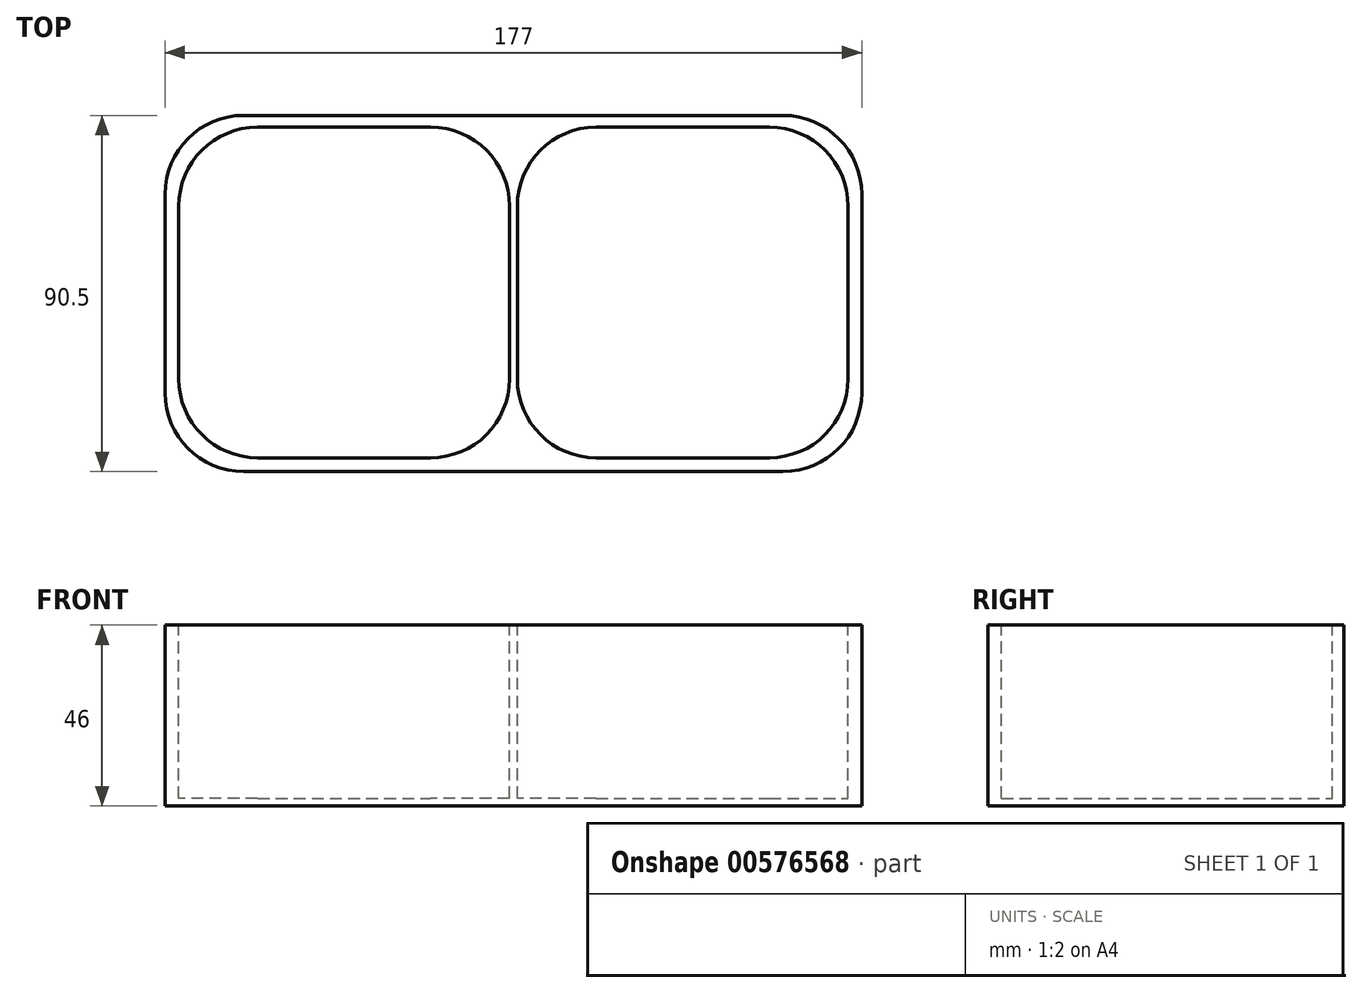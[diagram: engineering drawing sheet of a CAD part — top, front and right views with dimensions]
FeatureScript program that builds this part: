
annotation { "Feature Type Name" : "Feature", "Feature Type Description" : "" }
export const myFeature = defineFeature(function(context is Context, id is Id, definition is map)
    precondition{}
    {
        {
            var Q0;
            Q0=qCreatedBy(makeId("Top.planeOp"),FACE);
            var sketch = newSketch(context, id + "F0", { "sketchPlane" : qUnion([Q0])});
            skLineSegment(sketch, "E0.bottom", {"start": v(-97.24, 18.33) * mm, "end": v(-12.74, 18.33) * mm, "construction": true});
            skLineSegment(sketch, "E0.top", {"start": v(-97.24, -66.17) * mm, "end": v(-12.74, -66.17) * mm, "construction": true});
            skLineSegment(sketch, "E0.left", {"start": v(-97.24, 18.33) * mm, "end": v(-97.24, -66.17) * mm, "construction": true});
            skLineSegment(sketch, "E0.right", {"start": v(-12.74, 18.33) * mm, "end": v(-12.74, -66.17) * mm, "construction": true});
            skLineSegment(sketch, "E1.bottom", {"start": v(-10.74, 18.33) * mm, "end": v(73.76, 18.33) * mm, "construction": true});
            skLineSegment(sketch, "E1.top", {"start": v(-10.74, -66.17) * mm, "end": v(73.76, -66.17) * mm, "construction": true});
            skLineSegment(sketch, "E1.left", {"start": v(-10.74, 18.33) * mm, "end": v(-10.74, -66.17) * mm, "construction": true});
            skLineSegment(sketch, "E1.right", {"start": v(73.76, 18.33) * mm, "end": v(73.76, -66.17) * mm, "construction": true});
            skLineSegment(sketch, "E2.bottom", {"start": v(-100.24, 21.33) * mm, "end": v(76.76, 21.33) * mm});
            skLineSegment(sketch, "E2.top", {"start": v(-100.24, -69.17) * mm, "end": v(76.76, -69.17) * mm});
            skLineSegment(sketch, "E2.left", {"start": v(-100.24, 21.33) * mm, "end": v(-100.24, -69.17) * mm});
            skLineSegment(sketch, "E2.right", {"start": v(76.76, 21.33) * mm, "end": v(76.76, -69.17) * mm});
            skSolve(sketch);
        }
        {
            var Q0;
            Q0=makeQuery(id+"F0.imprint","IMPRINT",FACE,{"disambiguationData":[TD([[makeQuery(id+"F0.imprint","IMPRINT",EDGE,{"derivedFrom":sQuery(id+"F0.wireOp",EDGE,"E2.bottom")}),-1.0]])]});
            extrude(context, id + "F1", {"entities" : qUnion([Q0]), "oppositeDirection" : true, "depth" : 46 * mm, "offsetDistance" : 25 * mm});
        }
        {
            var Q0;
            Q0=makeQuery(id+"F1.opExtrude","CAP_FACE",FACE,{"disambiguationData":[OSD([sQuery(id+"F0.wireOp",EDGE,"E2.bottom"),sQuery(id+"F0.wireOp",EDGE,"E2.top"),sQuery(id+"F0.wireOp",EDGE,"E2.left"),sQuery(id+"F0.wireOp",EDGE,"E2.right")])],"isStart":true});
            var sketch = newSketch(context, id + "F2", { "sketchPlane" : qUnion([Q0])});
            skLineSegment(sketch, "E3.bottom", {"start": v(-96.74, 18.33) * mm, "end": v(-12.74, 18.33) * mm});
            skLineSegment(sketch, "E3.top", {"start": v(-96.74, -65.67) * mm, "end": v(-12.74, -65.67) * mm});
            skLineSegment(sketch, "E3.left", {"start": v(-96.74, 18.33) * mm, "end": v(-96.74, -65.67) * mm});
            skLineSegment(sketch, "E3.right", {"start": v(-12.74, 18.33) * mm, "end": v(-12.74, -65.67) * mm});
            skLineSegment(sketch, "E4.bottom", {"start": v(-10.74, -65.67) * mm, "end": v(73.26, -65.67) * mm});
            skLineSegment(sketch, "E4.top", {"start": v(-10.74, 18.33) * mm, "end": v(73.26, 18.33) * mm});
            skLineSegment(sketch, "E4.left", {"start": v(-10.74, -65.67) * mm, "end": v(-10.74, 18.33) * mm});
            skLineSegment(sketch, "E4.right", {"start": v(73.26, -65.67) * mm, "end": v(73.26, 18.33) * mm});
            skSolve(sketch);
        }
        {
            var Q0;
            Q0 = qSketchRegion(id + "F2", true);
            extrude(context, id + "F3", {"entities" : qUnion([Q0]), "operationType" : NewBodyOperationType.REMOVE, "oppositeDirection" : true, "depth" : 44 * mm, "offsetDistance" : 25 * mm});
        }
        {
            var Q0;
            Q0=makeQuery(id+"F3.boolean.opBoolean","COPY",EDGE,{"derivedFrom":makeQuery(id+"F3.opExtrude","SWEPT_EDGE",EDGE,{"disambiguationData":[OSD([sQuery(id+"F2.wireOp",EDGE,"E3.bottom"),sQuery(id+"F2.wireOp",EDGE,"E3.left")])]})});
            var Q1;
            Q1=makeQuery(id+"F3.boolean.opBoolean","COPY",EDGE,{"derivedFrom":makeQuery(id+"F3.opExtrude","SWEPT_EDGE",EDGE,{"disambiguationData":[OSD([sQuery(id+"F2.wireOp",EDGE,"E3.top"),sQuery(id+"F2.wireOp",EDGE,"E3.left")])]})});
            var Q2;
            Q2=makeQuery(id+"F3.boolean.opBoolean","COPY",EDGE,{"derivedFrom":makeQuery(id+"F3.opExtrude","SWEPT_EDGE",EDGE,{"disambiguationData":[OSD([sQuery(id+"F2.wireOp",EDGE,"E3.top"),sQuery(id+"F2.wireOp",EDGE,"E3.right")])]})});
            var Q3;
            Q3=makeQuery(id+"F3.boolean.opBoolean","COPY",EDGE,{"derivedFrom":makeQuery(id+"F3.opExtrude","SWEPT_EDGE",EDGE,{"disambiguationData":[OSD([sQuery(id+"F2.wireOp",EDGE,"E3.bottom"),sQuery(id+"F2.wireOp",EDGE,"E3.right")])]})});
            var Q4;
            Q4=makeQuery(id+"F3.boolean.opBoolean","COPY",EDGE,{"derivedFrom":makeQuery(id+"F3.opExtrude","SWEPT_EDGE",EDGE,{"disambiguationData":[OSD([sQuery(id+"F2.wireOp",EDGE,"E4.top"),sQuery(id+"F2.wireOp",EDGE,"E4.left")])]})});
            var Q5;
            Q5=makeQuery(id+"F3.boolean.opBoolean","COPY",EDGE,{"derivedFrom":makeQuery(id+"F3.opExtrude","SWEPT_EDGE",EDGE,{"disambiguationData":[OSD([sQuery(id+"F2.wireOp",EDGE,"E4.bottom"),sQuery(id+"F2.wireOp",EDGE,"E4.left")])]})});
            var Q6;
            Q6=makeQuery(id+"F3.boolean.opBoolean","COPY",EDGE,{"derivedFrom":makeQuery(id+"F3.opExtrude","SWEPT_EDGE",EDGE,{"disambiguationData":[OSD([sQuery(id+"F2.wireOp",EDGE,"E4.top"),sQuery(id+"F2.wireOp",EDGE,"E4.right")])]})});
            var Q7;
            Q7=makeQuery(id+"F3.boolean.opBoolean","COPY",EDGE,{"derivedFrom":makeQuery(id+"F3.opExtrude","SWEPT_EDGE",EDGE,{"disambiguationData":[OSD([sQuery(id+"F2.wireOp",EDGE,"E4.bottom"),sQuery(id+"F2.wireOp",EDGE,"E4.right")])]})});
            var Q8;
            Q8=makeQuery(id+"F1.opExtrude","SWEPT_EDGE",EDGE,{"disambiguationData":[OSD([sQuery(id+"F0.wireOp",EDGE,"E2.bottom"),sQuery(id+"F0.wireOp",EDGE,"E2.right")])]});
            var Q9;
            Q9=makeQuery(id+"F1.opExtrude","SWEPT_EDGE",EDGE,{"disambiguationData":[OSD([sQuery(id+"F0.wireOp",EDGE,"E2.bottom"),sQuery(id+"F0.wireOp",EDGE,"E2.left")])]});
            var Q10;
            Q10=makeQuery(id+"F1.opExtrude","SWEPT_EDGE",EDGE,{"disambiguationData":[OSD([sQuery(id+"F0.wireOp",EDGE,"E2.top"),sQuery(id+"F0.wireOp",EDGE,"E2.left")])]});
            var Q11;
            Q11=makeQuery(id+"F1.opExtrude","SWEPT_EDGE",EDGE,{"disambiguationData":[OSD([sQuery(id+"F0.wireOp",EDGE,"E2.top"),sQuery(id+"F0.wireOp",EDGE,"E2.right")])]});
            fillet(context, id + "F4", {"entities" : qUnion([Q0, Q1, Q2, Q3, Q4, Q5, Q6, Q7, Q8, Q9, Q10, Q11]), "radius" : 20 * mm, "tangentPropagation" : true, "allowEdgeOverflow" : false});
        }
    });
